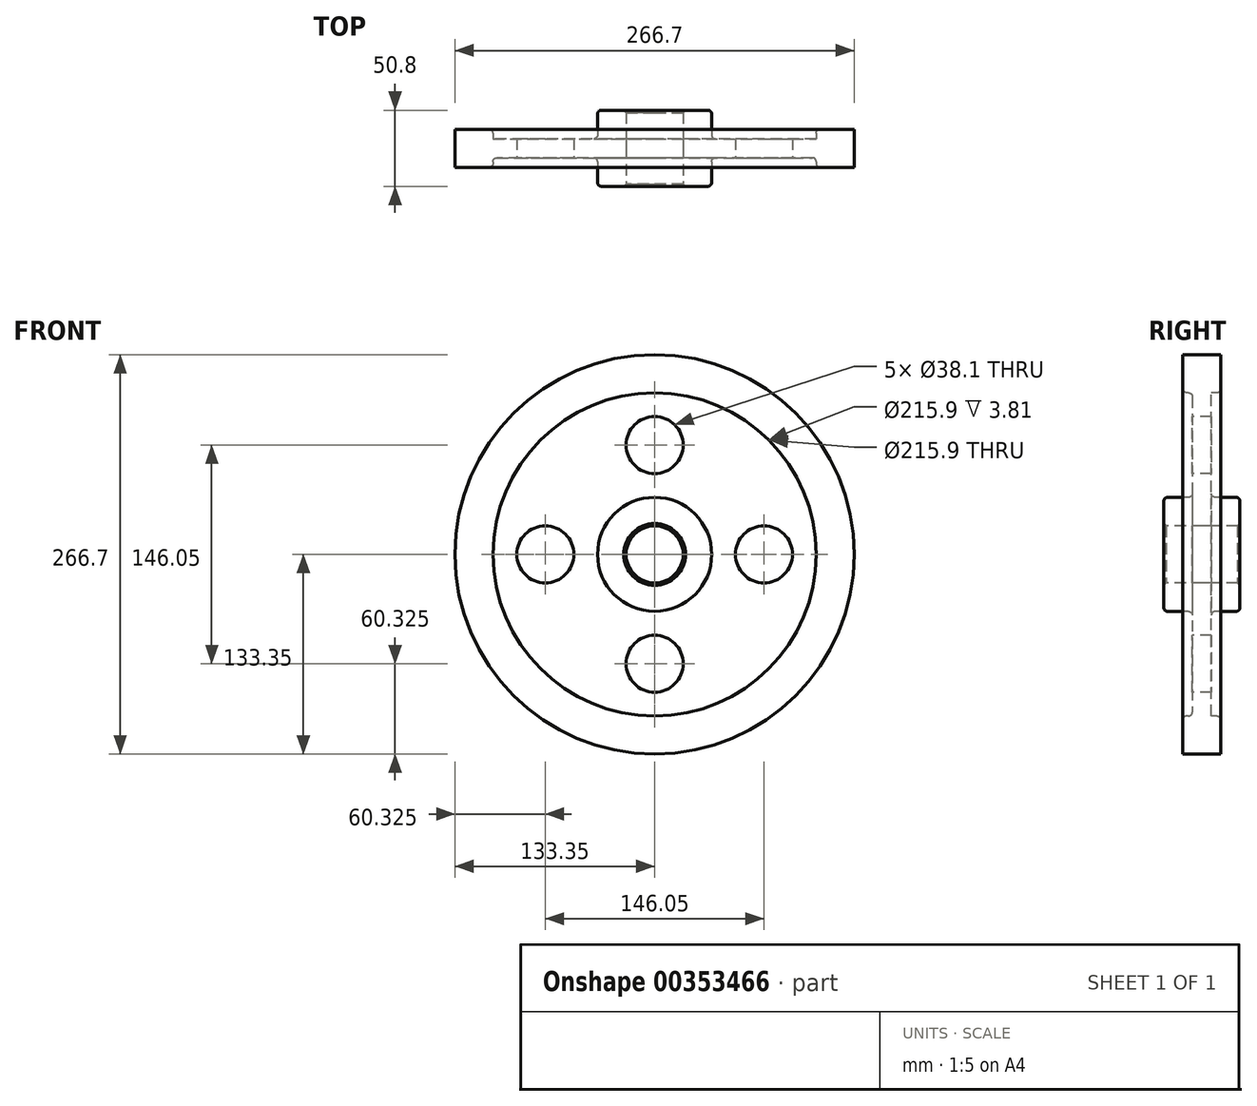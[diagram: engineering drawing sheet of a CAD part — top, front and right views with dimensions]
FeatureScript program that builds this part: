
annotation { "Feature Type Name" : "Feature", "Feature Type Description" : "" }
export const myFeature = defineFeature(function(context is Context, id is Id, definition is map)
    precondition{}
    {
        {
            var Q0;
            Q0=qCreatedBy(makeId("Right.planeOp"),FACE);
            var sketch = newSketch(context, id + "F0", { "sketchPlane" : qUnion([Q0])});
            skLineSegment(sketch, "E0", {"start": v(0, 0) * mm, "end": v(75.88, 0) * mm, "construction": true});
            skLineSegment(sketch, "E1.0", {"start": v(0, 19.05) * mm, "end": v(25.4, 19.05) * mm});
            skLineSegment(sketch, "E2.0", {"start": v(6.35, 38.1) * mm, "end": v(25.4, 38.1) * mm});
            skLineSegment(sketch, "E3.0", {"start": v(6.35, 107.95) * mm, "end": v(12.7, 107.95) * mm});
            skLineSegment(sketch, "E4.0", {"start": v(0, 133.35) * mm, "end": v(12.7, 133.35) * mm});
            skLineSegment(sketch, "E5", {"start": v(0, 133.35) * mm, "end": v(0, 0) * mm, "construction": true});
            skLineSegment(sketch, "E6.0", {"start": v(25.4, 38.1) * mm, "end": v(25.4, 19.05) * mm});
            skLineSegment(sketch, "E7.0", {"start": v(12.7, 133.35) * mm, "end": v(12.7, 107.95) * mm});
            skPoint(sketch, "E8.endSnap0", {"position": v(18.21, 56.11) * mm});
            skLineSegment(sketch, "E9.0", {"start": v(6.35, 107.95) * mm, "end": v(6.35, 38.1) * mm});
            skLineSegment(sketch, "E10.MirrorCS", {"start": v(0, 133.35) * mm, "end": v(-12.7, 133.35) * mm});
            skLineSegment(sketch, "E11.MirrorCS", {"start": v(-12.7, 133.35) * mm, "end": v(-12.7, 107.95) * mm});
            skLineSegment(sketch, "E12.MirrorCS", {"start": v(-6.35, 107.95) * mm, "end": v(-6.35, 38.1) * mm});
            skLineSegment(sketch, "E13.MirrorCS", {"start": v(-6.35, 38.1) * mm, "end": v(-25.4, 38.1) * mm});
            skLineSegment(sketch, "E14.MirrorCS", {"start": v(-25.4, 38.1) * mm, "end": v(-25.4, 19.05) * mm});
            skLineSegment(sketch, "E15.MirrorCS", {"start": v(0, 19.05) * mm, "end": v(-25.4, 19.05) * mm});
            skLineSegment(sketch, "E16.MirrorCS", {"start": v(-6.35, 107.95) * mm, "end": v(-12.7, 107.95) * mm});
            skSolve(sketch);
        }
        {
            var Q0;
            Q0=makeQuery(id+"F0.imprint","IMPRINT",FACE,{"disambiguationData":[TD([[makeQuery(id+"F0.imprint","IMPRINT",EDGE,{"derivedFrom":sQuery(id+"F0.wireOp",EDGE,"E1.0")}),1.0]])]});
            var Q1;
            Q1=sQuery(id+"F0.wireOp",EDGE,"E0");
            revolve(context, id + "F1", {"entities" : qUnion([Q0]), "axis" : qUnion([Q1]), "revolveType" : RevolveType.FULL});
        }
        {
            var Q0;
            Q0=makeQuery(id+"F1.opRevolve","SWEPT_FACE",FACE,{"disambiguationData":[OSD([sQuery(id+"F0.wireOp",EDGE,"E12.MirrorCS")])]});
            var sketch = newSketch(context, id + "F2", { "sketchPlane" : qUnion([Q0])});
            skLineSegment(sketch, "E17", {"start": v(0, 0) * mm, "end": v(0, 73.03) * mm});
            skCircle(sketch, "E18", {"center": v(0, 73.03) * mm, "radius": 19.05 * mm});
            skCircle(sketch, "E19.1.0", {"center": v(-73.03, 0) * mm, "radius": 19.05 * mm});
            skCircle(sketch, "E19.2.0", {"center": v(0, -73.03) * mm, "radius": 19.05 * mm});
            skCircle(sketch, "E19.3.0", {"center": v(73.03, 0) * mm, "radius": 19.05 * mm});
            skPoint(sketch, "E19.center", {"position": v(0, 0) * mm});
            skSolve(sketch);
        }
        {
            var Q0;
            Q0=makeQuery(id+"F2.imprint","IMPRINT",FACE,{"disambiguationData":[TD([[makeQuery(id+"F2.imprint","IMPRINT",EDGE,{"derivedFrom":sQuery(id+"F2.wireOp",EDGE,"E19.3.0")}),1.0]])]});
            var Q1;
            Q1=makeQuery(id+"F2.imprint","IMPRINT",FACE,{"disambiguationData":[TD([[makeQuery(id+"F2.imprint","IMPRINT",EDGE,{"derivedFrom":sQuery(id+"F2.wireOp",EDGE,"E18")}),1.0]])]});
            var Q2;
            Q2=makeQuery(id+"F2.imprint","IMPRINT",FACE,{"disambiguationData":[TD([[makeQuery(id+"F2.imprint","IMPRINT",EDGE,{"derivedFrom":sQuery(id+"F2.wireOp",EDGE,"E19.1.0")}),1.0]])]});
            var Q3;
            Q3=makeQuery(id+"F2.imprint","IMPRINT",FACE,{"disambiguationData":[TD([[makeQuery(id+"F2.imprint","IMPRINT",EDGE,{"derivedFrom":sQuery(id+"F2.wireOp",EDGE,"E19.2.0")}),1.0]])]});
            extrude(context, id + "F3", {"entities" : qUnion([Q0, Q1, Q2, Q3]), "operationType" : NewBodyOperationType.REMOVE, "oppositeDirection" : true, "depth" : 25.4 * mm});
        }
        {
            var Q0;
            Q0=makeQuery(id+"F1.opRevolve","SWEPT_EDGE",EDGE,{"disambiguationData":[OSD([sQuery(id+"F0.wireOp",EDGE,"E13.MirrorCS"),sQuery(id+"F0.wireOp",EDGE,"E14.MirrorCS")])]});
            var Q1;
            Q1=makeQuery(id+"F1.opRevolve","SWEPT_EDGE",EDGE,{"disambiguationData":[OSD([sQuery(id+"F0.wireOp",EDGE,"E12.MirrorCS"),sQuery(id+"F0.wireOp",EDGE,"E13.MirrorCS")])]});
            var Q2;
            Q2=makeQuery(id+"F1.opRevolve","SWEPT_EDGE",EDGE,{"disambiguationData":[OSD([sQuery(id+"F0.wireOp",EDGE,"E11.MirrorCS"),sQuery(id+"F0.wireOp",EDGE,"E16.MirrorCS")])]});
            var Q3;
            Q3=makeQuery(id+"F1.opRevolve","SWEPT_EDGE",EDGE,{"disambiguationData":[OSD([sQuery(id+"F0.wireOp",EDGE,"E12.MirrorCS"),sQuery(id+"F0.wireOp",EDGE,"E16.MirrorCS")])]});
            var Q4;
            Q4=makeQuery(id+"F1.opRevolve","SWEPT_EDGE",EDGE,{"disambiguationData":[OSD([sQuery(id+"F0.wireOp",EDGE,"E2.0"),sQuery(id+"F0.wireOp",EDGE,"E6.0")])]});
            var Q5;
            Q5=makeQuery(id+"F1.opRevolve","SWEPT_EDGE",EDGE,{"disambiguationData":[OSD([sQuery(id+"F0.wireOp",EDGE,"E2.0"),sQuery(id+"F0.wireOp",EDGE,"E9.0")])]});
            var Q6;
            Q6=makeQuery(id+"F1.opRevolve","SWEPT_EDGE",EDGE,{"disambiguationData":[OSD([sQuery(id+"F0.wireOp",EDGE,"E3.0"),sQuery(id+"F0.wireOp",EDGE,"E7.0")])]});
            fillet(context, id + "F4", {"entities" : qUnion([Q0, Q1, Q2, Q3, Q4, Q5, Q6]), "radius" : 2.54 * mm, "tangentPropagation" : true, "allowEdgeOverflow" : false});
        }
        {
            var Q0;
            Q0=makeQuery(id+"F1.opRevolve","SWEPT_EDGE",EDGE,{"disambiguationData":[OSD([sQuery(id+"F0.wireOp",EDGE,"E1.0"),sQuery(id+"F0.wireOp",EDGE,"E6.0")])]});
            var Q1;
            Q1=makeQuery(id+"F1.opRevolve","SWEPT_EDGE",EDGE,{"disambiguationData":[OSD([sQuery(id+"F0.wireOp",EDGE,"E14.MirrorCS"),sQuery(id+"F0.wireOp",EDGE,"E15.MirrorCS")])]});
            chamfer(context, id + "F5", {"entities" : qUnion([Q0, Q1]), "width" : 1.59 * mm, "tangentPropagation" : true});
        }
    });
